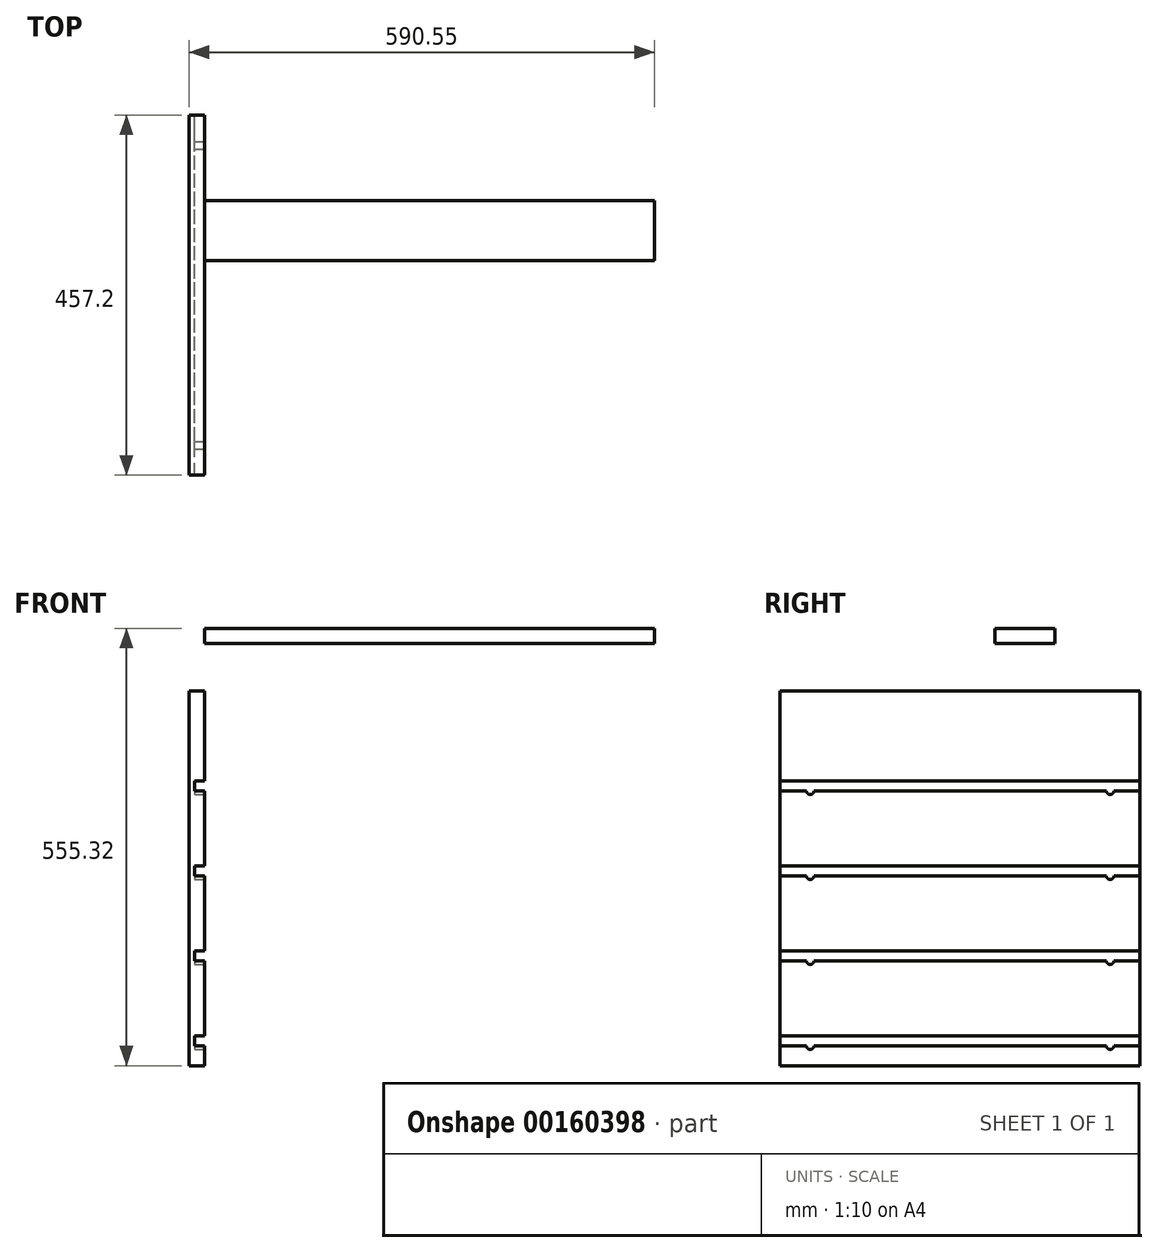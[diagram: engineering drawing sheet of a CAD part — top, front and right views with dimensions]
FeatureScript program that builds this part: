
annotation { "Feature Type Name" : "Feature", "Feature Type Description" : "" }
export const myFeature = defineFeature(function(context is Context, id is Id, definition is map)
    precondition{}
    {
        {
            var Q0;
            Q0=qCreatedBy(makeId("Right.planeOp"),FACE);
            var sketch = newSketch(context, id + "F0", { "sketchPlane" : qUnion([Q0])});
            skLineSegment(sketch, "E0.bottom", {"start": v(-394.71, 27.33) * mm, "end": v(62.49, 27.33) * mm});
            skLineSegment(sketch, "E0.top", {"start": v(-394.71, -448.92) * mm, "end": v(62.49, -448.92) * mm});
            skLineSegment(sketch, "E0.left", {"start": v(-394.71, 27.33) * mm, "end": v(-394.71, -448.92) * mm});
            skLineSegment(sketch, "E0.right", {"start": v(62.49, 27.33) * mm, "end": v(62.49, -448.92) * mm});
            skSolve(sketch);
        }
        {
            var Q0;
            Q0=qSketchRegion(id+"F0",true);
            var sketch = newSketch(context, id + "F1", { "sketchPlane" : qUnion([Q0])});
            skLineSegment(sketch, "E1.0", {"start": v(-394.71, -423.52) * mm, "end": v(-361.38, -423.52) * mm});
            skLineSegment(sketch, "E2.0", {"start": v(-394.71, -410.82) * mm, "end": v(62.49, -410.82) * mm});
            skArc(sketch, "E3", {"start": v(19.62, -423.52) * mm, "mid": v(24.39, -428.28) * mm, "end": v(29.15, -423.52) * mm});
            skLineSegment(sketch, "E4.trimOffspring", {"start": v(29.15, -423.52) * mm, "end": v(62.49, -423.52) * mm});
            skLineSegment(sketch, "E5.0.1.0", {"start": v(29.15, -315.57) * mm, "end": v(62.49, -315.57) * mm});
            skLineSegment(sketch, "E5.0.1.1", {"start": v(-394.71, -302.87) * mm, "end": v(62.49, -302.87) * mm});
            skLineSegment(sketch, "E5.0.1.2", {"start": v(-394.71, -315.57) * mm, "end": v(-361.38, -315.57) * mm});
            skArc(sketch, "E5.0.1.3", {"start": v(19.62, -315.57) * mm, "mid": v(24.39, -320.33) * mm, "end": v(29.15, -315.57) * mm});
            skLineSegment(sketch, "E5.0.2.0", {"start": v(29.15, -207.62) * mm, "end": v(62.49, -207.62) * mm});
            skLineSegment(sketch, "E5.0.2.1", {"start": v(-394.71, -194.92) * mm, "end": v(62.49, -194.92) * mm});
            skLineSegment(sketch, "E5.0.2.2", {"start": v(-394.71, -207.62) * mm, "end": v(-361.38, -207.62) * mm});
            skArc(sketch, "E5.0.2.3", {"start": v(19.62, -207.62) * mm, "mid": v(24.39, -212.38) * mm, "end": v(29.15, -207.62) * mm});
            skLineSegment(sketch, "E5.0.3.0", {"start": v(29.15, -99.67) * mm, "end": v(62.49, -99.67) * mm});
            skLineSegment(sketch, "E5.0.3.1", {"start": v(-394.71, -86.97) * mm, "end": v(62.49, -86.97) * mm});
            skLineSegment(sketch, "E5.0.3.2", {"start": v(-394.71, -99.67) * mm, "end": v(-361.38, -99.67) * mm});
            skArc(sketch, "E5.0.3.3", {"start": v(19.62, -99.67) * mm, "mid": v(24.39, -104.43) * mm, "end": v(29.15, -99.67) * mm});
            skLineSegment(sketch, "E5.direction1", {"start": v(-394.71, -410.82) * mm, "end": v(-369.31, -410.82) * mm, "construction": true});
            skLineSegment(sketch, "E5.direction2", {"start": v(-394.71, -410.82) * mm, "end": v(-394.71, -302.87) * mm, "construction": true});
            skPoint(sketch, "E6.centerSnap0", {"position": v(-356.61, 5.1) * mm});
            skArc(sketch, "E7", {"start": v(-361.38, -99.67) * mm, "mid": v(-356.61, -104.43) * mm, "end": v(-351.85, -99.67) * mm});
            skArc(sketch, "E8", {"start": v(-361.38, -207.62) * mm, "mid": v(-356.61, -212.38) * mm, "end": v(-351.85, -207.62) * mm});
            skArc(sketch, "E9", {"start": v(-361.38, -315.57) * mm, "mid": v(-356.61, -320.33) * mm, "end": v(-351.85, -315.57) * mm});
            skArc(sketch, "E10", {"start": v(-361.38, -423.52) * mm, "mid": v(-356.61, -428.28) * mm, "end": v(-351.85, -423.52) * mm});
            skLineSegment(sketch, "E11.trimOffspring", {"start": v(-351.85, -99.67) * mm, "end": v(19.62, -99.67) * mm});
            skLineSegment(sketch, "E12.trimOffspring", {"start": v(-351.85, -207.62) * mm, "end": v(19.62, -207.62) * mm});
            skLineSegment(sketch, "E13.trimOffspring", {"start": v(-351.85, -315.57) * mm, "end": v(19.62, -315.57) * mm});
            skLineSegment(sketch, "E14.trimOffspring", {"start": v(-351.85, -423.52) * mm, "end": v(19.62, -423.52) * mm});
            skLineSegment(sketch, "E15.trimOffspring", {"start": v(24.39, 20.98) * mm, "end": v(24.39, -448.92) * mm, "construction": true});
            skLineSegment(sketch, "E16.trimOffspring", {"start": v(-356.61, 20.98) * mm, "end": v(-356.61, -448.92) * mm, "construction": true});
            skSolve(sketch);
        }
        {
            var Q0;
            Q0=makeQuery(id+"F0.imprint","IMPRINT",FACE,{"disambiguationData":[TD([[makeQuery(id+"F0.imprint","IMPRINT",EDGE,{"derivedFrom":sQuery(id+"F0.wireOp",EDGE,"E0.bottom")}),-1.0]])]});
            extrude(context, id + "F2", {"entities" : qUnion([Q0]), "oppositeDirection" : true, "depth" : 19.05 * mm});
        }
        {
            var Q0;
            {var subQ2=sQuery(id+"F1.wireOp",EDGE,"E1.0");Q0=makeQuery(id+"F1.imprint","IMPRINT",FACE,{"disambiguationData":[TD([[makeQuery(id+"F1.imprint","IMPRINT",EDGE,{"derivedFrom":subQ2}),1.0]])]});}
            extrude(context, id + "F3", {"entities" : qUnion([Q0]), "operationType" : NewBodyOperationType.REMOVE, "oppositeDirection" : true, "depth" : 12.7 * mm});
        }
        {
            var Q0;
            {var subQ2=sQuery(id+"F1.wireOp",EDGE,"E5.0.1.0");Q0=makeQuery(id+"F1.imprint","IMPRINT",FACE,{"disambiguationData":[TD([[makeQuery(id+"F1.imprint","IMPRINT",EDGE,{"derivedFrom":subQ2}),1.0]])]});}
            var Q1;
            {var subQ2=sQuery(id+"F1.wireOp",EDGE,"E5.0.2.0");Q1=makeQuery(id+"F1.imprint","IMPRINT",FACE,{"disambiguationData":[TD([[makeQuery(id+"F1.imprint","IMPRINT",EDGE,{"derivedFrom":subQ2}),1.0]])]});}
            var Q2;
            {var subQ2=sQuery(id+"F1.wireOp",EDGE,"E5.0.3.0");Q2=makeQuery(id+"F1.imprint","IMPRINT",FACE,{"disambiguationData":[TD([[makeQuery(id+"F1.imprint","IMPRINT",EDGE,{"derivedFrom":subQ2}),1.0]])]});}
            var Q3;
            {var subQ2=sQuery(id+"F1.wireOp",EDGE,"E5.0.4.0");Q3=makeQuery(id+"F1.imprint","IMPRINT",FACE,{"disambiguationData":[TD([[makeQuery(id+"F1.imprint","IMPRINT",EDGE,{"derivedFrom":subQ2}),1.0]])]});}
            var Q4;
            {var subQ2=sQuery(id+"F1.wireOp",EDGE,"E5.0.5.0");Q4=makeQuery(id+"F1.imprint","IMPRINT",FACE,{"disambiguationData":[TD([[makeQuery(id+"F1.imprint","IMPRINT",EDGE,{"derivedFrom":subQ2}),1.0]])]});}
            var Q5;
            {var subQ2=sQuery(id+"F1.wireOp",EDGE,"E5.0.6.0");Q5=makeQuery(id+"F1.imprint","IMPRINT",FACE,{"disambiguationData":[TD([[makeQuery(id+"F1.imprint","IMPRINT",EDGE,{"derivedFrom":subQ2}),1.0]])]});}
            var Q6;
            {var subQ2=sQuery(id+"F1.wireOp",EDGE,"E5.0.7.0");Q6=makeQuery(id+"F1.imprint","IMPRINT",FACE,{"disambiguationData":[TD([[makeQuery(id+"F1.imprint","IMPRINT",EDGE,{"derivedFrom":subQ2}),1.0]])]});}
            var Q7;
            Q7=qBodyType(qCreatedBy(id+"F1",EDGE),BodyType.WIRE);
            var Q8;
            Q8=sQuery(id+"F1.wireOp",EDGE,"E5.0.1.2");
            extrude(context, id + "F4", {"entities" : qUnion([Q0, Q1, Q2, Q3, Q4, Q5, Q6]), "operationType" : NewBodyOperationType.REMOVE, "surfaceEntities" : qUnion([Q7, Q8]), "oppositeDirection" : true, "depth" : 12.7 * mm});
        }
        {
            var Q0;
            Q0=qCreatedBy(makeId("Right.planeOp"),FACE);
            var sketch = newSketch(context, id + "F5", { "sketchPlane" : qUnion([Q0])});
            skLineSegment(sketch, "E17.bottom", {"start": v(-45.84, 87.35) * mm, "end": v(-122.04, 87.35) * mm});
            skLineSegment(sketch, "E17.top", {"start": v(-45.84, 106.4) * mm, "end": v(-122.04, 106.4) * mm});
            skLineSegment(sketch, "E17.left", {"start": v(-45.84, 87.35) * mm, "end": v(-45.84, 106.4) * mm});
            skLineSegment(sketch, "E17.right", {"start": v(-122.04, 87.35) * mm, "end": v(-122.04, 106.4) * mm});
            skSolve(sketch);
        }
        {
            var Q0;
            Q0=qSketchRegion(id+"F5",true);
            extrude(context, id + "F6", {"entities" : qUnion([Q0]), "depth" : 571.5 * mm});
        }
    });
